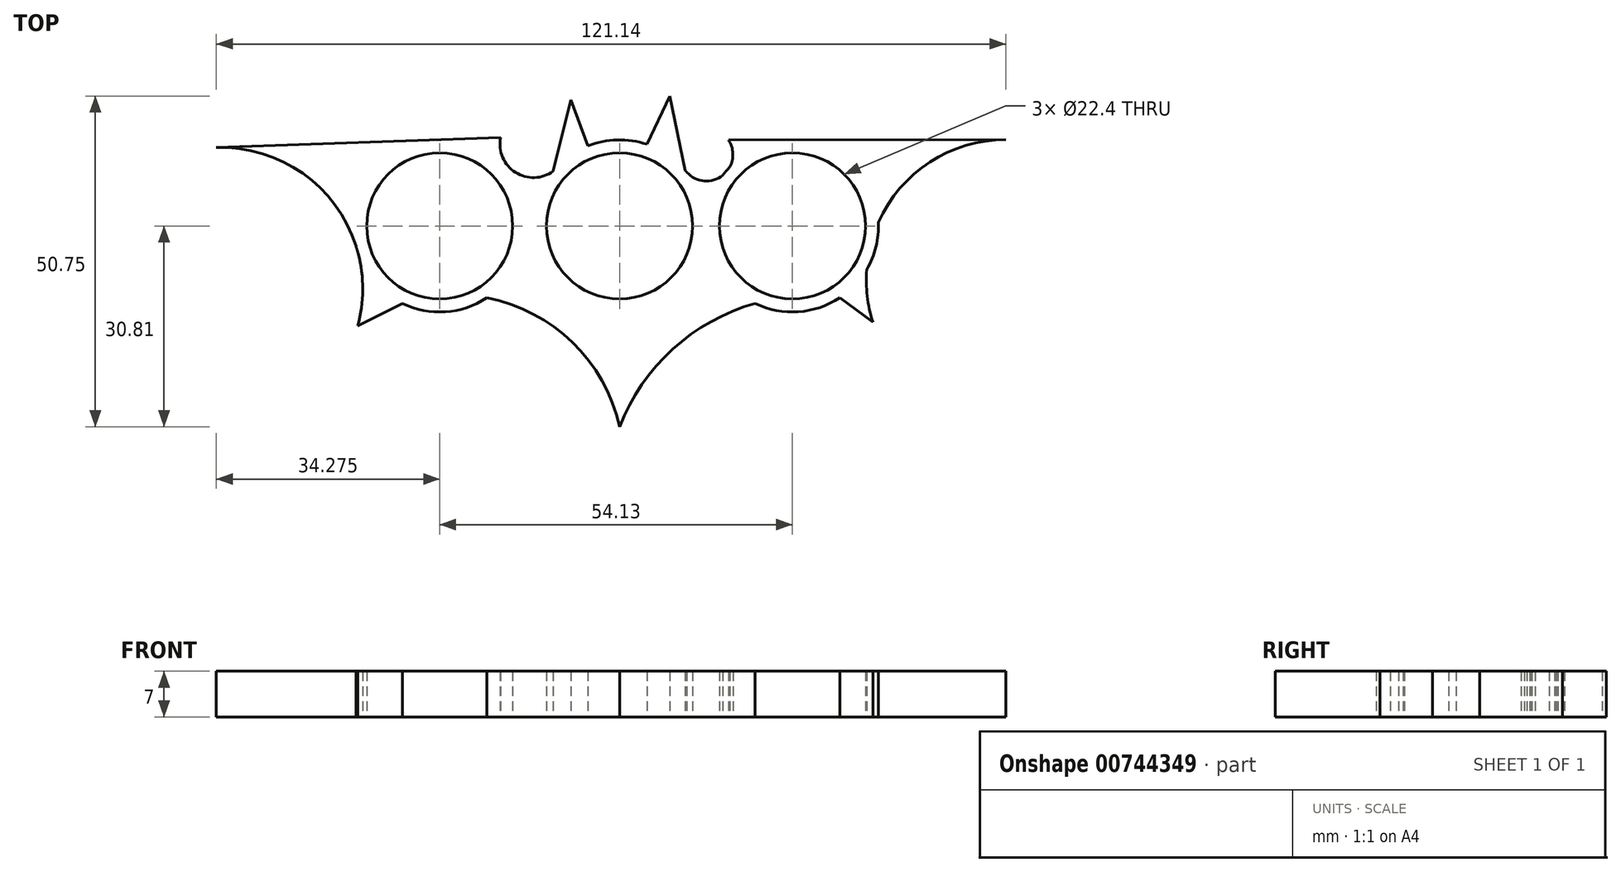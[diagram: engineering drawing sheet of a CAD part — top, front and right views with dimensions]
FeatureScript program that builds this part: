
annotation { "Feature Type Name" : "Feature", "Feature Type Description" : "" }
export const myFeature = defineFeature(function(context is Context, id is Id, definition is map)
    precondition{}
    {
        {
            var Q0;
            Q0=qCreatedBy(makeId("Top.planeOp"),FACE);
            var sketch = newSketch(context, id + "F0", { "sketchPlane" : qUnion([Q0])});
            skCircle(sketch, "E0", {"center": v(0, 0) * mm, "radius": 11.2 * mm});
            skCircle(sketch, "E1", {"center": v(0, 0) * mm, "radius": 13.2 * mm});
            skCircle(sketch, "E2", {"center": v(-27.6, 0) * mm, "radius": 11.2 * mm});
            skCircle(sketch, "E3", {"center": v(-27.6, 0) * mm, "radius": 13.2 * mm});
            skCircle(sketch, "E4", {"center": v(26.54, 0) * mm, "radius": 11.2 * mm});
            skCircle(sketch, "E5", {"center": v(26.54, 0) * mm, "radius": 13.2 * mm});
            skArc(sketch, "E6", {"start": v(0, -30.8) * mm, "mid": v(-12.46, -13.94) * mm, "end": v(-33.34, -11.89) * mm});
            skArc(sketch, "E7", {"start": v(33.81, -11.01) * mm, "mid": v(13.46, -15.02) * mm, "end": v(0, -30.8) * mm});
            skLineSegment(sketch, "E8", {"start": v(-33.34, -11.89) * mm, "end": v(-40.15, -15.33) * mm});
            skLineSegment(sketch, "E9", {"start": v(-61.87, 12.03) * mm, "end": v(-18.25, 13.53) * mm});
            skArc(sketch, "E10", {"start": v(-40.15, -15.33) * mm, "mid": v(-44.12, 3.83) * mm, "end": v(-61.87, 12.03) * mm});
            skArc(sketch, "E11", {"start": v(-18.25, 13.53) * mm, "mid": v(-15.97, 8.2) * mm, "end": v(-10.17, 8.4) * mm});
            skLineSegment(sketch, "E12", {"start": v(-10.17, 8.4) * mm, "end": v(-7.47, 19.36) * mm});
            skLineSegment(sketch, "E13", {"start": v(-7.47, 19.36) * mm, "end": v(-4.83, 12.28) * mm});
            skLineSegment(sketch, "E14", {"start": v(33.81, -11.01) * mm, "end": v(38.87, -14.74) * mm});
            skLineSegment(sketch, "E15", {"start": v(59.27, 13.24) * mm, "end": v(16.72, 13.19) * mm});
            skArc(sketch, "E16", {"start": v(59.27, 13.24) * mm, "mid": v(41.97, 4.43) * mm, "end": v(38.87, -14.74) * mm});
            skArc(sketch, "E17", {"start": v(10.07, 8.53) * mm, "mid": v(15.67, 7.62) * mm, "end": v(16.72, 13.19) * mm});
            skLineSegment(sketch, "E18", {"start": v(10.07, 8.53) * mm, "end": v(7.69, 19.94) * mm});
            skLineSegment(sketch, "E19", {"start": v(7.69, 19.94) * mm, "end": v(4.19, 12.52) * mm});
            skSolve(sketch);
        }
        {
            var Q0;
            Q0 = qSketchRegion(id + "F0", true);
            extrude(context, id + "F1", {"entities" : qUnion([Q0]), "depth" : 7 * mm, "offsetDistance" : 25 * mm});
        }
    });
